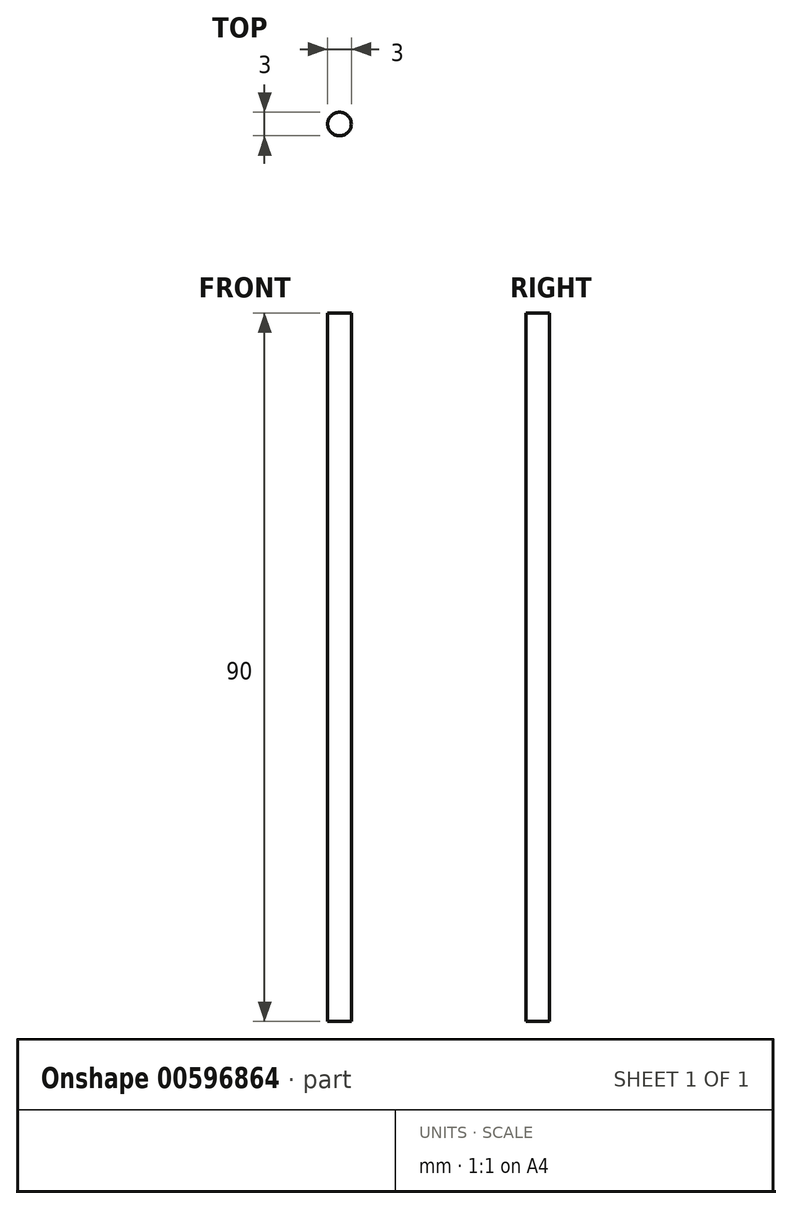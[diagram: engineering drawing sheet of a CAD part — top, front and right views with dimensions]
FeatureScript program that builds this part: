
annotation { "Feature Type Name" : "Feature", "Feature Type Description" : "" }
export const myFeature = defineFeature(function(context is Context, id is Id, definition is map)
    precondition{}
    {
        {
            var Q0;
            Q0=qCreatedBy(makeId("Front.planeOp"),FACE);
            var sketch = newSketch(context, id + "F0", { "sketchPlane" : qUnion([Q0])});
            skLineSegment(sketch, "E0.bottom", {"start": v(-47.69, 66.14) * mm, "end": v(-46.19, 66.14) * mm});
            skLineSegment(sketch, "E0.top", {"start": v(-47.69, -23.86) * mm, "end": v(-46.19, -23.86) * mm});
            skLineSegment(sketch, "E0.left", {"start": v(-47.69, 66.14) * mm, "end": v(-47.69, -23.86) * mm});
            skLineSegment(sketch, "E0.right", {"start": v(-46.19, 66.14) * mm, "end": v(-46.19, -23.86) * mm});
            skSolve(sketch);
        }
        {
            var Q0;
            Q0=makeQuery(id+"F0.imprint","IMPRINT",FACE,{"disambiguationData":[TD([[makeQuery(id+"F0.imprint","IMPRINT",EDGE,{"derivedFrom":sQuery(id+"F0.wireOp",EDGE,"E0.bottom")}),-1.0]])]});
            var Q1;
            Q1=sQuery(id+"F0.wireOp",EDGE,"E0.left");
            revolve(context, id + "F1", {"surfaceOperationType" : NewSurfaceOperationType.NEW, "entities" : qUnion([Q0]), "axis" : qUnion([Q1]), "revolveType" : RevolveType.FULL});
        }
    });
